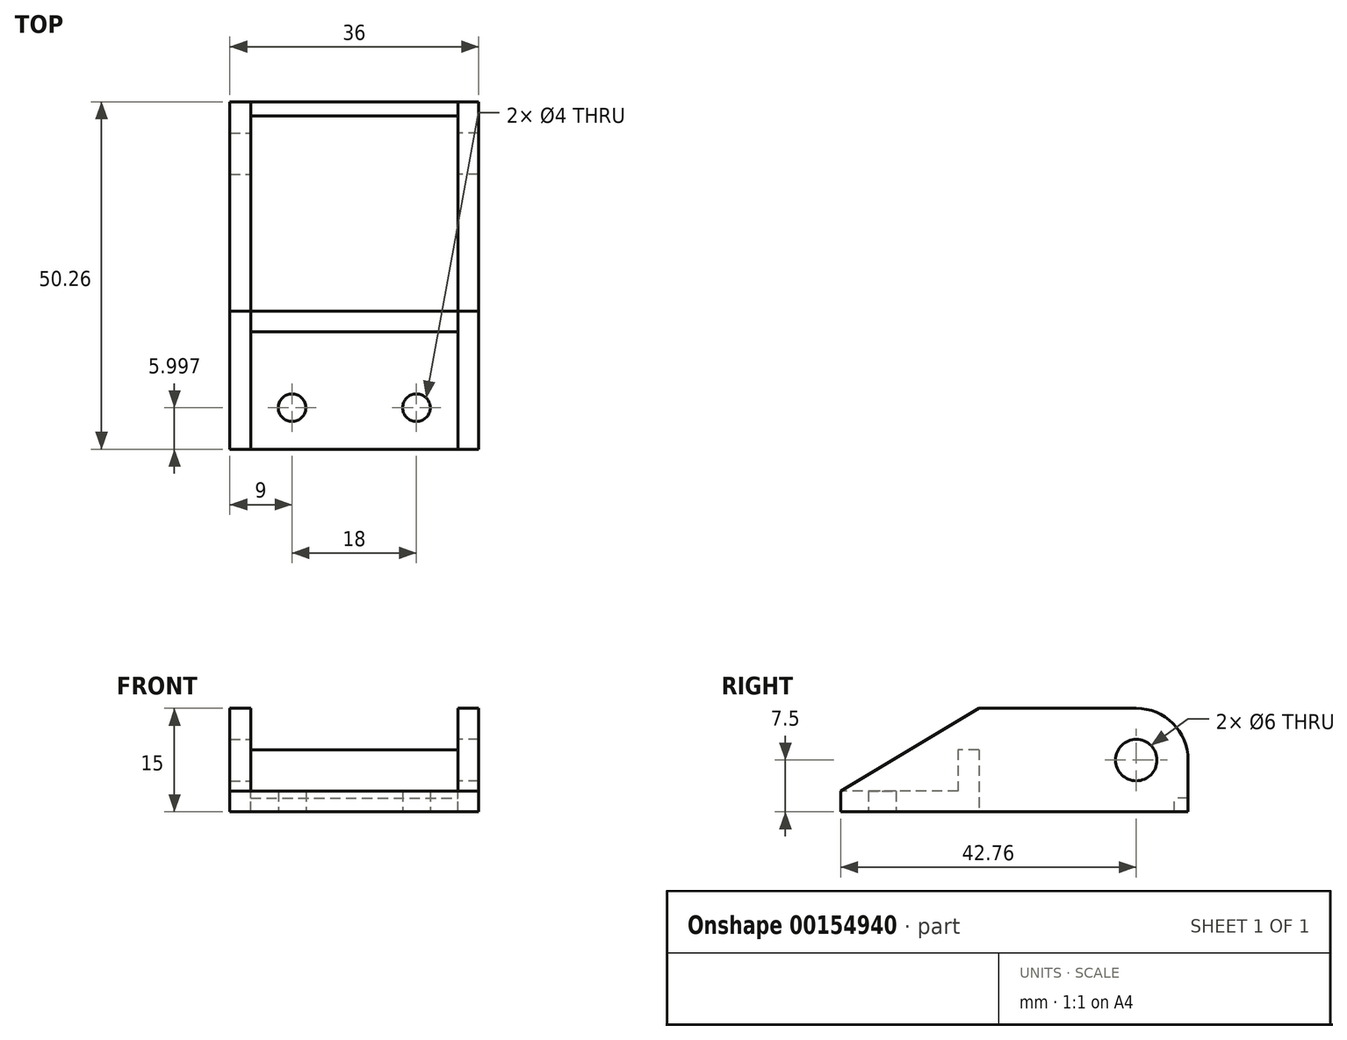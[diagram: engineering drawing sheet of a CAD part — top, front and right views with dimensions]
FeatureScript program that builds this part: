
annotation { "Feature Type Name" : "Feature", "Feature Type Description" : "" }
export const myFeature = defineFeature(function(context is Context, id is Id, definition is map)
    precondition{}
    {
        {
            var Q0;
            Q0=qCreatedBy(makeId("Top.planeOp"),FACE);
            var sketch = newSketch(context, id + "F0", { "sketchPlane" : qUnion([Q0])});
            skLineSegment(sketch, "E0.bottom", {"start": v(0, 9.74) * mm, "end": v(15, 9.74) * mm});
            skLineSegment(sketch, "E0.top", {"start": v(0, -10.26) * mm, "end": v(15, -10.26) * mm});
            skLineSegment(sketch, "E0.right", {"start": v(15, 9.74) * mm, "end": v(15, -10.26) * mm});
            skCircle(sketch, "E1", {"center": v(9, -4.26) * mm, "radius": 2 * mm});
            skLineSegment(sketch, "E2", {"start": v(0, -10.26) * mm, "end": v(0, 9.74) * mm});
            skSolve(sketch);
        }
        {
            var Q0;
            Q0=makeQuery(id+"F0.imprint","IMPRINT",FACE,{"disambiguationData":[TD([[makeQuery(id+"F0.imprint","IMPRINT",EDGE,{"derivedFrom":sQuery(id+"F0.wireOp",EDGE,"E0.bottom")}),-1.0]])]});
            extrude(context, id + "F1", {"entities" : qUnion([Q0]), "depth" : 3 * mm});
        }
        {
            var Q0;
            Q0=makeQuery(id+"F1.opExtrude","SWEPT_FACE",FACE,{"disambiguationData":[OSD([sQuery(id+"F0.wireOp",EDGE,"E0.right")])]});
            var sketch = newSketch(context, id + "F2", { "sketchPlane" : qUnion([Q0])});
            skLineSegment(sketch, "E3.bottom", {"start": v(0, 0) * mm, "end": v(40, 0) * mm});
            skLineSegment(sketch, "E3.top", {"start": v(9.74, 15) * mm, "end": v(32.5, 15) * mm});
            skLineSegment(sketch, "E3.right", {"start": v(40, 0) * mm, "end": v(40, 7.5) * mm});
            skCircle(sketch, "E4", {"center": v(32.5, 7.5) * mm, "radius": 3 * mm});
            skArc(sketch, "E5", {"start": v(40, 7.5) * mm, "mid": v(37.8, 12.8) * mm, "end": v(32.5, 15) * mm});
            skLineSegment(sketch, "E6", {"start": v(-10.26, 0) * mm, "end": v(-10.26, 3) * mm});
            skLineSegment(sketch, "E7", {"start": v(0, 0) * mm, "end": v(-10.26, 0) * mm});
            skLineSegment(sketch, "E8", {"start": v(9.74, 0) * mm, "end": v(9.74, 15) * mm});
            skLineSegment(sketch, "E9", {"start": v(9.74, 15) * mm, "end": v(-10.26, 3) * mm});
            skSolve(sketch);
        }
        {
            var Q0;
            Q0 = qSketchRegion(id + "F2", true);
            extrude(context, id + "F3", {"entities" : qUnion([Q0]), "operationType" : NewBodyOperationType.ADD, "depth" : 3 * mm});
        }
        {
            var Q0;
            Q0=makeQuery(id+"F1.opExtrude","SWEPT_BODY",BODY,{"disambiguationData":[OSD([sQuery(id+"F0.wireOp",EDGE,"E0.bottom"),sQuery(id+"F0.wireOp",EDGE,"E0.top"),sQuery(id+"F0.wireOp",EDGE,"E0.right"),sQuery(id+"F0.wireOp",EDGE,"E1"),sQuery(id+"F0.wireOp",EDGE,"E2")])]});
            var Q1;
            Q1=qCreatedBy(makeId("Right.planeOp"),FACE);
            mirror(context, id + "F4", {"operationType" : NewBodyOperationType.ADD, "entities" : qUnion([Q0]), "mirrorPlane" : qUnion([Q1])});
        }
        {
            var Q0;
            {var subQ0=makeQuery(id+"F1.opExtrude","CAP_FACE",FACE,{"disambiguationData":[OSD([sQuery(id+"F0.wireOp",EDGE,"E0.bottom"),sQuery(id+"F0.wireOp",EDGE,"E0.top"),sQuery(id+"F0.wireOp",EDGE,"E0.right"),sQuery(id+"F0.wireOp",EDGE,"E1"),sQuery(id+"F0.wireOp",EDGE,"E2")])],"isStart":false});Q0=makeQuery(id+"F4.boolean.opBoolean","MERGE",FACE,{"derivedFrom":[subQ0,makeQuery(id+"F4.opPattern","COPY",FACE,{"derivedFrom":subQ0,"instanceName":"1"})]});}
            var sketch = newSketch(context, id + "F5", { "sketchPlane" : qUnion([Q0])});
            skLineSegment(sketch, "E10.bottom", {"start": v(-15, 9.74) * mm, "end": v(15, 9.74) * mm});
            skLineSegment(sketch, "E10.top", {"start": v(-15, 6.74) * mm, "end": v(15, 6.74) * mm});
            skLineSegment(sketch, "E10.left", {"start": v(-15, 9.74) * mm, "end": v(-15, 6.74) * mm});
            skLineSegment(sketch, "E10.right", {"start": v(15, 9.74) * mm, "end": v(15, 6.74) * mm});
            skSolve(sketch);
        }
        {
            var Q0;
            Q0=makeQuery(id+"F5.imprint","IMPRINT",FACE,{"disambiguationData":[TD([[makeQuery(id+"F5.imprint","IMPRINT",EDGE,{"derivedFrom":sQuery(id+"F5.wireOp",EDGE,"E10.bottom")}),-1.0]])]});
            extrude(context, id + "F6", {"entities" : qUnion([Q0]), "operationType" : NewBodyOperationType.ADD, "depth" : 6 * mm});
        }
        {
            var Q0;
            Q0=makeQuery(id+"F3.opExtrude","CAP_FACE",FACE,{"disambiguationData":[OSD([sQuery(id+"F2.wireOp",EDGE,"E3.bottom"),sQuery(id+"F2.wireOp",EDGE,"E3.top"),sQuery(id+"F2.wireOp",EDGE,"E3.right"),sQuery(id+"F2.wireOp",EDGE,"E4"),sQuery(id+"F2.wireOp",EDGE,"E5"),sQuery(id+"F2.wireOp",EDGE,"E6"),sQuery(id+"F2.wireOp",EDGE,"E7"),sQuery(id+"F2.wireOp",EDGE,"E9")])],"isStart":true});
            var sketch = newSketch(context, id + "F7", { "sketchPlane" : qUnion([Q0])});
            skLineSegment(sketch, "E11.bottom", {"start": v(-40, 0) * mm, "end": v(-38, 0) * mm});
            skLineSegment(sketch, "E11.top", {"start": v(-40, 2) * mm, "end": v(-38, 2) * mm});
            skLineSegment(sketch, "E11.left", {"start": v(-40, 0) * mm, "end": v(-40, 2) * mm});
            skLineSegment(sketch, "E11.right", {"start": v(-38, 0) * mm, "end": v(-38, 2) * mm});
            skSolve(sketch);
        }
        {
            var Q0;
            Q0=makeQuery(id+"F7.imprint","IMPRINT",FACE,{"disambiguationData":[TD([[makeQuery(id+"F7.imprint","IMPRINT",EDGE,{"derivedFrom":sQuery(id+"F7.wireOp",EDGE,"E11.bottom")}),1.0]])]});
            extrude(context, id + "F8", {"entities" : qUnion([Q0]), "operationType" : NewBodyOperationType.ADD, "endBound" : BoundingType.UP_TO_NEXT, "depth" : 25.4 * mm});
        }
    });
